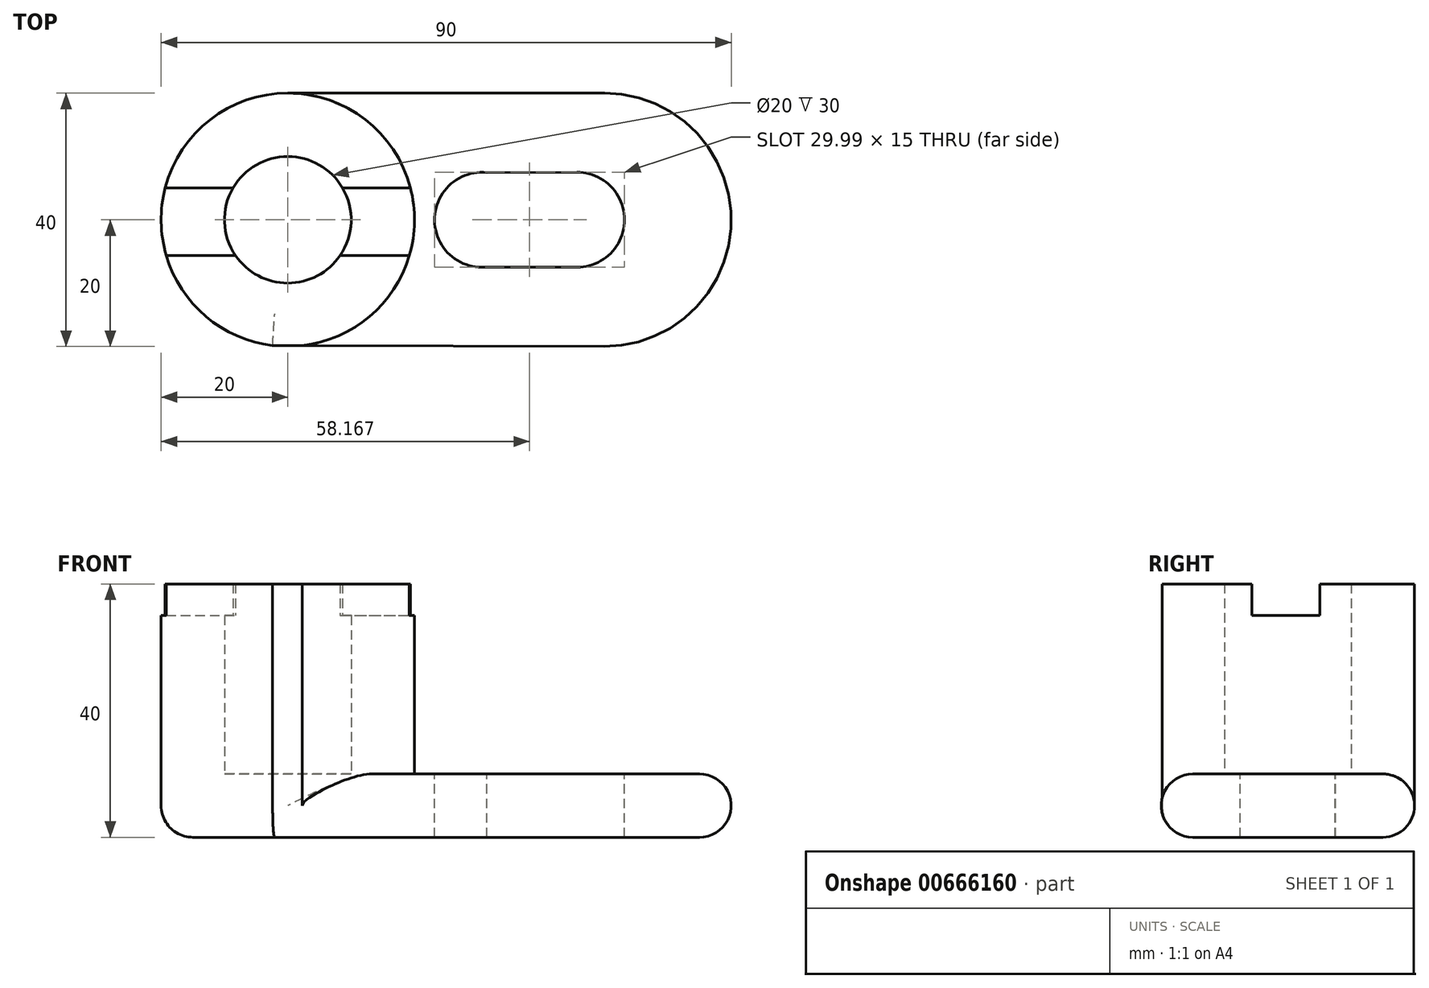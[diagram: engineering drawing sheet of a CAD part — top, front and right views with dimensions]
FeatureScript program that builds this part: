
annotation { "Feature Type Name" : "Feature", "Feature Type Description" : "" }
export const myFeature = defineFeature(function(context is Context, id is Id, definition is map)
    precondition{}
    {
        {
            var Q0;
            Q0=qCreatedBy(makeId("Top.planeOp"),FACE);
            var sketch = newSketch(context, id + "F0", { "sketchPlane" : qUnion([Q0])});
            skArc(sketch, "E0", {"start": v(0, 20) * mm, "mid": v(-19.97, -1.15) * mm, "end": v(2.3, -19.87) * mm});
            skArc(sketch, "E1", {"start": v(49.94, -20) * mm, "mid": v(70, -0.03) * mm, "end": v(50, 20) * mm});
            skLineSegment(sketch, "E2", {"start": v(0, 20) * mm, "end": v(50, 20) * mm});
            skLineSegment(sketch, "E3", {"start": v(-2.4, -19.86) * mm, "end": v(49.94, -20) * mm});
            skSolve(sketch);
        }
        {
            var Q0;
            {var subQ5=sQuery(id+"F0.wireOp",EDGE,"E1");Q0=makeQuery(id+"F0.imprint","IMPRINT",FACE,{"disambiguationData":[TD([[makeQuery(id+"F0.imprint","IMPRINT",EDGE,{"derivedFrom":subQ5}),1.0]])]});}
            extrude(context, id + "F1", {"entities" : qUnion([Q0]), "depth" : 10 * mm, "offsetDistance" : 25 * mm});
        }
        {
            var Q0;
            Q0=makeQuery(id+"F1.opExtrude","CAP_FACE",FACE,{"disambiguationData":[OSD([sQuery(id+"F0.wireOp",EDGE,"E0"),sQuery(id+"F0.wireOp",EDGE,"E1"),sQuery(id+"F0.wireOp",EDGE,"E2"),sQuery(id+"F0.wireOp",EDGE,"E3")])],"isStart":false});
            var sketch = newSketch(context, id + "F2", { "sketchPlane" : qUnion([Q0])});
            skCircle(sketch, "E4", {"center": v(0, 0) * mm, "radius": 20 * mm});
            skCircle(sketch, "E5", {"center": v(0, 0) * mm, "radius": 10 * mm});
            skSolve(sketch);
        }
        {
            var Q0;
            Q0=makeQuery(id+"F2.imprint","IMPRINT",FACE,{"disambiguationData":[TD([[makeQuery(id+"F2.imprint","IMPRINT",EDGE,{"derivedFrom":sQuery(id+"F2.wireOp",EDGE,"E5")}),-1.0]])]});
            extrude(context, id + "F3", {"entities" : qUnion([Q0]), "operationType" : NewBodyOperationType.ADD, "depth" : 30 * mm, "offsetDistance" : 25 * mm});
        }
        {
            var Q0;
            Q0=makeQuery(id+"F3.opExtrude","CAP_FACE",FACE,{"disambiguationData":[OSD([sQuery(id+"F0.wireOp",EDGE,"E3"),sQuery(id+"F2.wireOp",EDGE,"E4"),sQuery(id+"F2.wireOp",EDGE,"E5")])],"isStart":false});
            var sketch = newSketch(context, id + "F4", { "sketchPlane" : qUnion([Q0])});
            skLineSegment(sketch, "E6.bottom", {"start": v(-23.13, 5.06) * mm, "end": v(20.96, 5.06) * mm});
            skLineSegment(sketch, "E6.top", {"start": v(-23.13, -5.65) * mm, "end": v(20.96, -5.65) * mm});
            skLineSegment(sketch, "E6.left", {"start": v(-23.13, 5.06) * mm, "end": v(-23.13, -5.65) * mm});
            skLineSegment(sketch, "E6.right", {"start": v(20.96, 5.06) * mm, "end": v(20.96, -5.65) * mm});
            skSolve(sketch);
        }
        {
            var Q0;
            Q0 = qSketchRegion(id + "F4", true);
            extrude(context, id + "F5", {"entities" : qUnion([Q0]), "operationType" : NewBodyOperationType.REMOVE, "oppositeDirection" : true, "depth" : 5 * mm, "offsetDistance" : 25 * mm});
        }
        {
            var Q0;
            {var subQ0=sQuery(id+"F0.wireOp",EDGE,"E2");var subQ1=sQuery(id+"F0.wireOp",EDGE,"E1");var subQ2=sQuery(id+"F0.wireOp",EDGE,"E3");var subQ3=sQuery(id+"F0.wireOp",EDGE,"E0");Q0=makeQuery(id+"F3.boolean.opBoolean","SPLIT",FACE,{"disambiguationData":[TD([makeQuery(id+"F1.opExtrude","SWEPT_FACE",FACE,{"disambiguationData":[OSD([subQ3])]})])],"derivedFrom":makeQuery(id+"F1.opExtrude","CAP_FACE",FACE,{"disambiguationData":[OSD([subQ3,subQ1,subQ0,subQ2])],"isStart":false})});}
            var sketch = newSketch(context, id + "F6", { "sketchPlane" : qUnion([Q0])});
            skArc(sketch, "E7", {"start": v(31.4, 7.46) * mm, "mid": v(23.17, 0.36) * mm, "end": v(30.69, -7.5) * mm});
            skArc(sketch, "E8", {"start": v(45.66, -7.5) * mm, "mid": v(53.16, 0) * mm, "end": v(45.64, 7.5) * mm});
            skLineSegment(sketch, "E9", {"start": v(29.89, 7.46) * mm, "end": v(45.64, 7.5) * mm});
            skLineSegment(sketch, "E10", {"start": v(30.64, -7.5) * mm, "end": v(45.66, -7.5) * mm});
            skSolve(sketch);
        }
        {
            var Q0;
            {var subQ0=sQuery(id+"F6.wireOp",EDGE,"E9");var subQ1=sQuery(id+"F6.wireOp",EDGE,"E7");var subQ2=makeQuery(id+"F6.imprint","INTERSECT",VERTEX,{"disambiguationData":[OD(0.0)],"derivedFrom":[subQ1,subQ0]});Q0=makeQuery(id+"F6.imprint","IMPRINT",FACE,{"disambiguationData":[TD([[makeQuery(id+"F6.imprint","IMPRINT",EDGE,{"disambiguationData":[TD([[subQ2,-1.0]])],"derivedFrom":subQ1}),1.0]])]});}
            var Q1;
            {var subQ3=sQuery(id+"F6.wireOp",EDGE,"E8");Q1=makeQuery(id+"F6.imprint","IMPRINT",FACE,{"disambiguationData":[TD([[makeQuery(id+"F6.imprint","IMPRINT",EDGE,{"derivedFrom":subQ3}),1.0]])]});}
            extrude(context, id + "F7", {"entities" : qUnion([Q0, Q1]), "operationType" : NewBodyOperationType.REMOVE, "oppositeDirection" : true, "depth" : 25 * mm, "offsetDistance" : 25 * mm});
        }
        {
            var Q0;
            Q0=makeQuery(id+"F1.opExtrude","CAP_EDGE",EDGE,{"disambiguationData":[OSD([sQuery(id+"F0.wireOp",EDGE,"E2")])],"isStart":true});
            var Q1;
            Q1=makeQuery(id+"F1.opExtrude","CAP_EDGE",EDGE,{"disambiguationData":[OSD([sQuery(id+"F0.wireOp",EDGE,"E3")])],"isStart":false});
            var Q2;
            Q2=makeQuery(id+"F3.opExtrude","CAP_EDGE",EDGE,{"disambiguationData":[OSD([sQuery(id+"F2.wireOp",EDGE,"E4")])],"isStart":true});
            fillet(context, id + "F8", {"entities" : qUnion([Q0, Q1, Q2]), "radius" : 5 * mm, "tangentPropagation" : true, "allowEdgeOverflow" : false});
        }
    });
